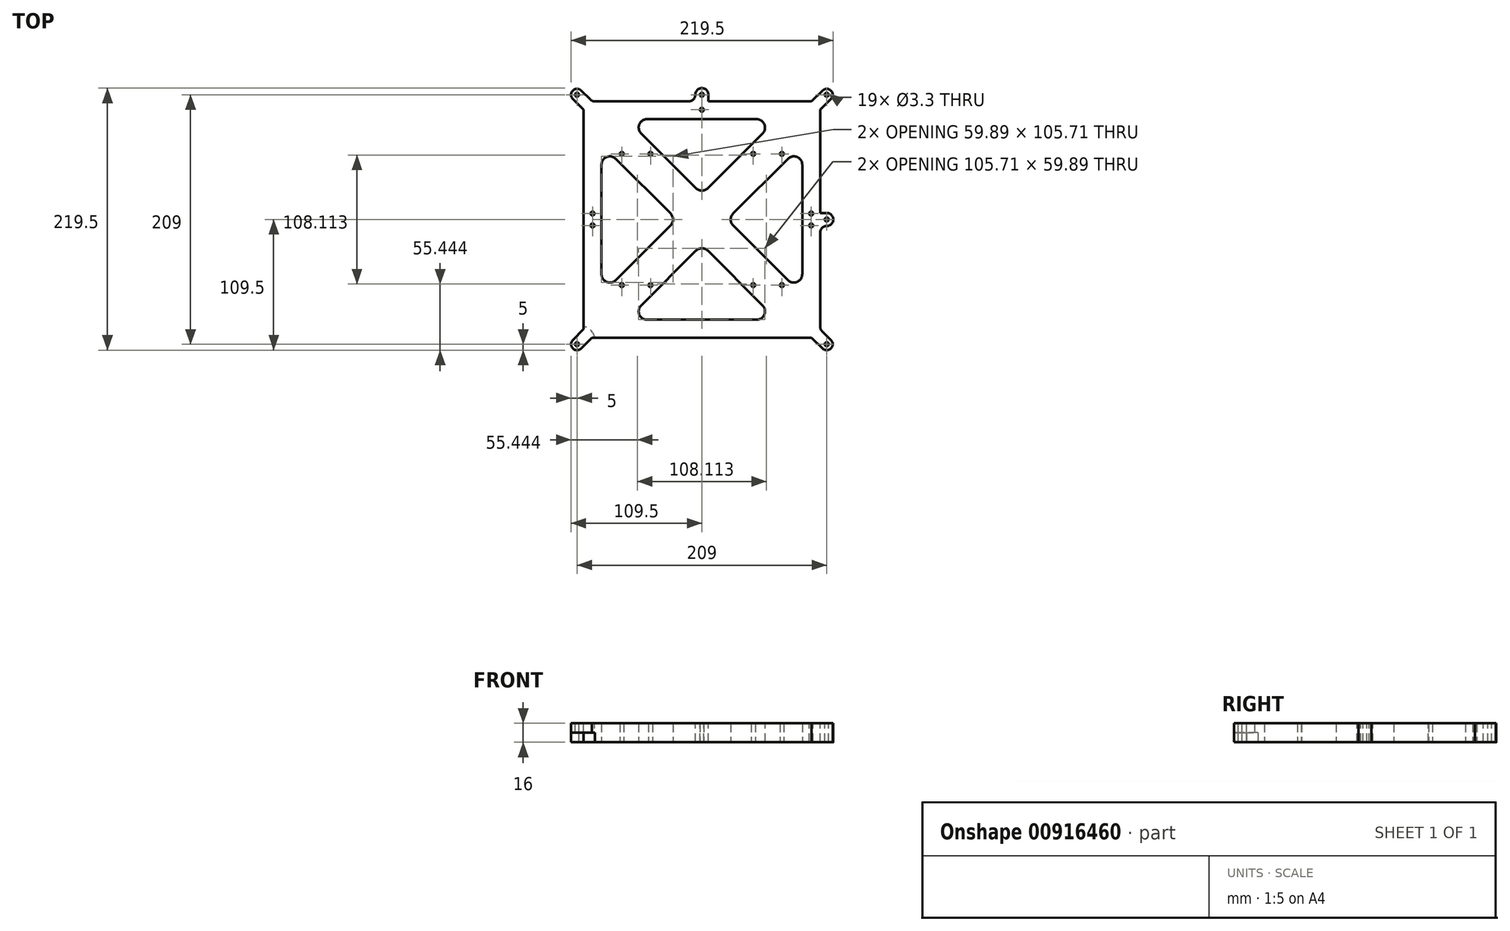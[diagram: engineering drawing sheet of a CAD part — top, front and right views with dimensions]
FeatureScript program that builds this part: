
annotation { "Feature Type Name" : "Feature", "Feature Type Description" : "" }
export const myFeature = defineFeature(function(context is Context, id is Id, definition is map)
    precondition{}
    {
        {
            var Q0;
            Q0=qCreatedBy(makeId("Top.planeOp"),FACE);
            var sketch = newSketch(context, id + "F0", { "sketchPlane" : qUnion([Q0])});
            skLineSegment(sketch, "E0.bottom", {"start": v(99, 99) * mm, "end": v(-99, 99) * mm});
            skLineSegment(sketch, "E0.top", {"start": v(99, -99) * mm, "end": v(-99, -99) * mm});
            skLineSegment(sketch, "E0.left", {"start": v(99, 99) * mm, "end": v(99, -99) * mm});
            skLineSegment(sketch, "E0.right", {"start": v(-99, 99) * mm, "end": v(-99, -99) * mm});
            skPoint(sketch, "E0.middle", {"position": v(0, 0) * mm});
            skLineSegment(sketch, "E1", {"start": v(99, 99) * mm, "end": v(-99, -99) * mm, "construction": true});
            skLineSegment(sketch, "E2", {"start": v(0, 21.21) * mm, "end": v(62.79, 84) * mm});
            skLineSegment(sketch, "E3.MirrorCS", {"start": v(0, 21.21) * mm, "end": v(-62.79, 84) * mm});
            skLineSegment(sketch, "E4", {"start": v(62.79, 84) * mm, "end": v(-62.79, 84) * mm});
            skLineSegment(sketch, "E5", {"start": v(-99, 99) * mm, "end": v(99, -99) * mm, "construction": true});
            skLineSegment(sketch, "E6.MirrorCS", {"start": v(-21.21, 0) * mm, "end": v(-84, 62.79) * mm});
            skLineSegment(sketch, "E7.MirrorCS", {"start": v(-84, -62.79) * mm, "end": v(-84, 62.79) * mm});
            skLineSegment(sketch, "E8.MirrorCS", {"start": v(-21.21, 0) * mm, "end": v(-84, -62.79) * mm});
            skLineSegment(sketch, "E9.MirrorCS", {"start": v(21.21, 0) * mm, "end": v(84, 62.79) * mm});
            skLineSegment(sketch, "E10.MirrorCS", {"start": v(84, 62.79) * mm, "end": v(84, -62.79) * mm});
            skLineSegment(sketch, "E11.MirrorCS", {"start": v(21.21, 0) * mm, "end": v(84, -62.79) * mm});
            skLineSegment(sketch, "E12.MirrorCS", {"start": v(0, -21.21) * mm, "end": v(-62.79, -84) * mm});
            skLineSegment(sketch, "E13.MirrorCS", {"start": v(0, -21.21) * mm, "end": v(62.79, -84) * mm});
            skLineSegment(sketch, "E14.MirrorCS", {"start": v(-62.79, -84) * mm, "end": v(62.79, -84) * mm});
            skLineSegment(sketch, "E15", {"start": v(-55, 55) * mm, "end": v(-43, 55) * mm, "construction": true});
            skLineSegment(sketch, "E16", {"start": v(-55, 55) * mm, "end": v(-67, 55) * mm, "construction": true});
            skLineSegment(sketch, "E17.MirrorCS", {"start": v(55, 55) * mm, "end": v(67, 55) * mm, "construction": true});
            skLineSegment(sketch, "E18.MirrorCS", {"start": v(55, 55) * mm, "end": v(43, 55) * mm, "construction": true});
            skLineSegment(sketch, "E19.MirrorCS", {"start": v(55, -55) * mm, "end": v(67, -55) * mm, "construction": true});
            skLineSegment(sketch, "E20.MirrorCS", {"start": v(-55, -55) * mm, "end": v(-43, -55) * mm, "construction": true});
            skLineSegment(sketch, "E21.MirrorCS", {"start": v(-55, -55) * mm, "end": v(-67, -55) * mm, "construction": true});
            skLineSegment(sketch, "E22.MirrorCS", {"start": v(55, -55) * mm, "end": v(43, -55) * mm, "construction": true});
            skSolve(sketch);
        }
        {
            var Q0;
            Q0=makeQuery(id+"F0.imprint","IMPRINT",FACE,{"disambiguationData":[TD([[makeQuery(id+"F0.imprint","IMPRINT",EDGE,{"derivedFrom":sQuery(id+"F0.wireOp",EDGE,"E0.bottom")}),1.0]])]});
            extrude(context, id + "F1", {"entities" : qUnion([Q0]), "depth" : 16 * mm});
        }
        {
            var Q0;
            Q0=makeQuery(id+"F1.opExtrude","CAP_FACE",FACE,{"disambiguationData":[OSD([sQuery(id+"F0.wireOp",EDGE,"E0.bottom"),sQuery(id+"F0.wireOp",EDGE,"E0.top"),sQuery(id+"F0.wireOp",EDGE,"E0.left"),sQuery(id+"F0.wireOp",EDGE,"E0.right"),sQuery(id+"F0.wireOp",EDGE,"E2"),sQuery(id+"F0.wireOp",EDGE,"E3.MirrorCS"),sQuery(id+"F0.wireOp",EDGE,"E4"),sQuery(id+"F0.wireOp",EDGE,"E6.MirrorCS"),sQuery(id+"F0.wireOp",EDGE,"E7.MirrorCS"),sQuery(id+"F0.wireOp",EDGE,"E8.MirrorCS"),sQuery(id+"F0.wireOp",EDGE,"E9.MirrorCS"),sQuery(id+"F0.wireOp",EDGE,"E10.MirrorCS"),sQuery(id+"F0.wireOp",EDGE,"E11.MirrorCS"),sQuery(id+"F0.wireOp",EDGE,"E12.MirrorCS"),sQuery(id+"F0.wireOp",EDGE,"E13.MirrorCS"),sQuery(id+"F0.wireOp",EDGE,"E14.MirrorCS")])],"isStart":false});
            var sketch = newSketch(context, id + "F2", { "sketchPlane" : qUnion([Q0])});
            skLineSegment(sketch, "E23", {"start": v(-99, 99) * mm, "end": v(-104.5, 104.5) * mm, "construction": true});
            skLineSegment(sketch, "E24.0", {"start": v(-91.93, 99) * mm, "end": v(-100.96, 108.04) * mm});
            skLineSegment(sketch, "E25.0", {"start": v(-99, 91.93) * mm, "end": v(-108.04, 100.96) * mm});
            skArc(sketch, "E26", {"start": v(-108.04, 100.96) * mm, "mid": v(-108.04, 108.04) * mm, "end": v(-100.96, 108.04) * mm});
            skLineSegment(sketch, "E27.MirrorCS", {"start": v(99, 91.93) * mm, "end": v(108.04, 100.96) * mm});
            skLineSegment(sketch, "E28.MirrorCS", {"start": v(99, 99) * mm, "end": v(104.5, 104.5) * mm, "construction": true});
            skLineSegment(sketch, "E29.MirrorCS", {"start": v(91.93, 99) * mm, "end": v(100.96, 108.04) * mm});
            skArc(sketch, "E30.MirrorCS", {"start": v(108.04, 100.96) * mm, "mid": v(108.04, 108.04) * mm, "end": v(100.96, 108.04) * mm});
            skLineSegment(sketch, "E31.MirrorCS", {"start": v(99, -99) * mm, "end": v(104.5, -104.5) * mm, "construction": true});
            skLineSegment(sketch, "E32.MirrorCS", {"start": v(-99, -99) * mm, "end": v(-104.5, -104.5) * mm, "construction": true});
            skLineSegment(sketch, "E33.MirrorCS", {"start": v(-99, -91.93) * mm, "end": v(-108.04, -100.96) * mm});
            skLineSegment(sketch, "E34.MirrorCS", {"start": v(91.93, -99) * mm, "end": v(100.96, -108.04) * mm});
            skArc(sketch, "E35.MirrorCS", {"start": v(108.04, -100.96) * mm, "mid": v(108.04, -108.04) * mm, "end": v(100.96, -108.04) * mm});
            skLineSegment(sketch, "E36.MirrorCS", {"start": v(99, -91.93) * mm, "end": v(108.04, -100.96) * mm});
            skArc(sketch, "E37.MirrorCS", {"start": v(-108.04, -100.96) * mm, "mid": v(-108.04, -108.04) * mm, "end": v(-100.96, -108.04) * mm});
            skLineSegment(sketch, "E38.MirrorCS", {"start": v(-91.93, -99) * mm, "end": v(-100.96, -108.04) * mm});
            skLineSegment(sketch, "E39", {"start": v(-5.5, 99) * mm, "end": v(-5.5, 110) * mm});
            skLineSegment(sketch, "E40", {"start": v(-5.5, 110) * mm, "end": v(5.5, 110) * mm});
            skLineSegment(sketch, "E41", {"start": v(5.5, 110) * mm, "end": v(5.5, 99) * mm});
            skLineSegment(sketch, "E42", {"start": v(99, 5.5) * mm, "end": v(110, 5.5) * mm});
            skLineSegment(sketch, "E43", {"start": v(110, 5.5) * mm, "end": v(110, -5.5) * mm});
            skLineSegment(sketch, "E44", {"start": v(110, -5.5) * mm, "end": v(99, -5.5) * mm});
            skLineSegment(sketch, "E45", {"start": v(110, 0) * mm, "end": v(99, 0) * mm, "construction": true});
            skLineSegment(sketch, "E46", {"start": v(0, 110) * mm, "end": v(0, 99) * mm, "construction": true});
            skLineSegment(sketch, "E47", {"start": v(0, 104.5) * mm, "end": v(5.5, 110) * mm, "construction": true});
            skLineSegment(sketch, "E48", {"start": v(104.5, 0) * mm, "end": v(110, -5.5) * mm, "construction": true});
            skLineSegment(sketch, "E49", {"start": v(91.5, 5) * mm, "end": v(91.5, -5) * mm});
            skLineSegment(sketch, "E50", {"start": v(-91.5, 5) * mm, "end": v(-91.5, -5) * mm});
            skSolve(sketch);
        }
        {
            var Q0;
            {var subQ4=sQuery(id+"F2.wireOp",EDGE,"E33.MirrorCS");Q0=makeQuery(id+"F2.imprint","IMPRINT",FACE,{"disambiguationData":[TD([[makeQuery(id+"F2.imprint","IMPRINT",EDGE,{"derivedFrom":subQ4}),1.0]])]});}
            var Q1;
            {var subQ3=sQuery(id+"F2.wireOp",EDGE,"E34.MirrorCS");Q1=makeQuery(id+"F2.imprint","IMPRINT",FACE,{"disambiguationData":[TD([[makeQuery(id+"F2.imprint","IMPRINT",EDGE,{"derivedFrom":subQ3}),1.0]])]});}
            var Q2;
            {var subQ0=sQuery(id+"F2.wireOp",EDGE,"E42");Q2=makeQuery(id+"F2.imprint","IMPRINT",FACE,{"disambiguationData":[TD([[makeQuery(id+"F2.imprint","IMPRINT",EDGE,{"derivedFrom":subQ0}),-1.0]])]});}
            var Q3;
            {var subQ4=sQuery(id+"F2.wireOp",EDGE,"E27.MirrorCS");Q3=makeQuery(id+"F2.imprint","IMPRINT",FACE,{"disambiguationData":[TD([[makeQuery(id+"F2.imprint","IMPRINT",EDGE,{"derivedFrom":subQ4}),1.0]])]});}
            var Q4;
            {var subQ3=sQuery(id+"F2.wireOp",EDGE,"E24.0");Q4=makeQuery(id+"F2.imprint","IMPRINT",FACE,{"disambiguationData":[TD([[makeQuery(id+"F2.imprint","IMPRINT",EDGE,{"derivedFrom":subQ3}),1.0]])]});}
            var Q5;
            {var subQ0=sQuery(id+"F2.wireOp",EDGE,"E39");Q5=makeQuery(id+"F2.imprint","IMPRINT",FACE,{"disambiguationData":[TD([[makeQuery(id+"F2.imprint","IMPRINT",EDGE,{"derivedFrom":subQ0}),-1.0]])]});}
            var Q6;
            Q6=makeQuery(id+"F1.opExtrude","CAP_FACE",FACE,{"disambiguationData":[OSD([sQuery(id+"F0.wireOp",EDGE,"E0.bottom"),sQuery(id+"F0.wireOp",EDGE,"E0.top"),sQuery(id+"F0.wireOp",EDGE,"E0.left"),sQuery(id+"F0.wireOp",EDGE,"E0.right"),sQuery(id+"F0.wireOp",EDGE,"E2"),sQuery(id+"F0.wireOp",EDGE,"E3.MirrorCS"),sQuery(id+"F0.wireOp",EDGE,"E4"),sQuery(id+"F0.wireOp",EDGE,"E6.MirrorCS"),sQuery(id+"F0.wireOp",EDGE,"E7.MirrorCS"),sQuery(id+"F0.wireOp",EDGE,"E8.MirrorCS"),sQuery(id+"F0.wireOp",EDGE,"E9.MirrorCS"),sQuery(id+"F0.wireOp",EDGE,"E10.MirrorCS"),sQuery(id+"F0.wireOp",EDGE,"E11.MirrorCS"),sQuery(id+"F0.wireOp",EDGE,"E12.MirrorCS"),sQuery(id+"F0.wireOp",EDGE,"E13.MirrorCS"),sQuery(id+"F0.wireOp",EDGE,"E14.MirrorCS")])],"isStart":true});
            extrude(context, id + "F3", {"entities" : qUnion([Q0, Q1, Q2, Q3, Q4, Q5]), "operationType" : NewBodyOperationType.ADD, "endBound" : BoundingType.UP_TO_SURFACE, "oppositeDirection" : true, "endBoundEntityFace" : qUnion([Q6]), "depth" : 25 * mm});
        }
        {
            var Q0;
            {var subQ0=sQuery(id+"F0.wireOp",EDGE,"E0.left");var subQ1=sQuery(id+"F0.wireOp",EDGE,"E14.MirrorCS");var subQ2=sQuery(id+"F0.wireOp",EDGE,"E13.MirrorCS");var subQ3=sQuery(id+"F0.wireOp",EDGE,"E12.MirrorCS");var subQ4=sQuery(id+"F0.wireOp",EDGE,"E11.MirrorCS");var subQ5=sQuery(id+"F0.wireOp",EDGE,"E10.MirrorCS");var subQ6=sQuery(id+"F0.wireOp",EDGE,"E9.MirrorCS");var subQ7=sQuery(id+"F0.wireOp",EDGE,"E8.MirrorCS");var subQ8=sQuery(id+"F0.wireOp",EDGE,"E7.MirrorCS");var subQ9=sQuery(id+"F0.wireOp",EDGE,"E6.MirrorCS");var subQ10=sQuery(id+"F0.wireOp",EDGE,"E4");var subQ11=sQuery(id+"F0.wireOp",EDGE,"E3.MirrorCS");var subQ12=sQuery(id+"F0.wireOp",EDGE,"E2");var subQ13=sQuery(id+"F0.wireOp",EDGE,"E0.right");var subQ14=sQuery(id+"F0.wireOp",EDGE,"E0.top");var subQ15=sQuery(id+"F0.wireOp",EDGE,"E0.bottom");Q0=makeQuery(id+"F3.boolean.opBoolean","MERGE",FACE,{"derivedFrom":[makeQuery(id+"F1.opExtrude","CAP_FACE",FACE,{"disambiguationData":[OSD([subQ15,subQ14,subQ0,subQ13,subQ12,subQ11,subQ10,subQ9,subQ8,subQ7,subQ6,subQ5,subQ4,subQ3,subQ2,subQ1])],"isStart":true}),makeQuery(id+"F3.opExtrude","CAP_FACE",FACE,{"disambiguationData":[OSD([subQ15,subQ14,subQ0,subQ13,subQ12,subQ11,subQ10,subQ9,subQ8,subQ7,subQ6,subQ5,subQ4,subQ3,subQ2,subQ1]),ownerDisambiguation([makeQuery(id+"F3.opExtrude","SWEPT_BODY",BODY,{"disambiguationData":[OSD([subQ15,subQ13,sQuery(id+"F2.wireOp",EDGE,"E24.0"),sQuery(id+"F2.wireOp",EDGE,"E25.0"),sQuery(id+"F2.wireOp",EDGE,"E26")])]})])],"isStart":false}),makeQuery(id+"F3.opExtrude","CAP_FACE",FACE,{"disambiguationData":[OSD([subQ15,subQ14,subQ0,subQ13,subQ12,subQ11,subQ10,subQ9,subQ8,subQ7,subQ6,subQ5,subQ4,subQ3,subQ2,subQ1]),ownerDisambiguation([makeQuery(id+"F3.opExtrude","SWEPT_BODY",BODY,{"disambiguationData":[OSD([subQ15,subQ0,sQuery(id+"F2.wireOp",EDGE,"E27.MirrorCS"),sQuery(id+"F2.wireOp",EDGE,"E29.MirrorCS"),sQuery(id+"F2.wireOp",EDGE,"E30.MirrorCS")])]})])],"isStart":false}),makeQuery(id+"F3.opExtrude","CAP_FACE",FACE,{"disambiguationData":[OSD([subQ15,subQ14,subQ0,subQ13,subQ12,subQ11,subQ10,subQ9,subQ8,subQ7,subQ6,subQ5,subQ4,subQ3,subQ2,subQ1]),ownerDisambiguation([makeQuery(id+"F3.opExtrude","SWEPT_BODY",BODY,{"disambiguationData":[OSD([subQ14,subQ13,sQuery(id+"F2.wireOp",EDGE,"E33.MirrorCS"),sQuery(id+"F2.wireOp",EDGE,"E37.MirrorCS"),sQuery(id+"F2.wireOp",EDGE,"E38.MirrorCS")])]})])],"isStart":false}),makeQuery(id+"F3.opExtrude","CAP_FACE",FACE,{"disambiguationData":[OSD([subQ15,subQ14,subQ0,subQ13,subQ12,subQ11,subQ10,subQ9,subQ8,subQ7,subQ6,subQ5,subQ4,subQ3,subQ2,subQ1]),ownerDisambiguation([makeQuery(id+"F3.opExtrude","SWEPT_BODY",BODY,{"disambiguationData":[OSD([subQ14,subQ0,sQuery(id+"F2.wireOp",EDGE,"E34.MirrorCS"),sQuery(id+"F2.wireOp",EDGE,"E35.MirrorCS"),sQuery(id+"F2.wireOp",EDGE,"E36.MirrorCS")])]})])],"isStart":false}),makeQuery(id+"F3.opExtrude","CAP_FACE",FACE,{"disambiguationData":[OSD([subQ15,subQ14,subQ0,subQ13,subQ12,subQ11,subQ10,subQ9,subQ8,subQ7,subQ6,subQ5,subQ4,subQ3,subQ2,subQ1]),ownerDisambiguation([makeQuery(id+"F3.opExtrude","SWEPT_BODY",BODY,{"disambiguationData":[OSD([subQ15,sQuery(id+"F2.wireOp",EDGE,"E39"),sQuery(id+"F2.wireOp",EDGE,"E40"),sQuery(id+"F2.wireOp",EDGE,"E41")])]})])],"isStart":false}),makeQuery(id+"F3.opExtrude","CAP_FACE",FACE,{"disambiguationData":[OSD([subQ15,subQ14,subQ0,subQ13,subQ12,subQ11,subQ10,subQ9,subQ8,subQ7,subQ6,subQ5,subQ4,subQ3,subQ2,subQ1]),ownerDisambiguation([makeQuery(id+"F3.opExtrude","SWEPT_BODY",BODY,{"disambiguationData":[OSD([subQ0,sQuery(id+"F2.wireOp",EDGE,"E42"),sQuery(id+"F2.wireOp",EDGE,"E43"),sQuery(id+"F2.wireOp",EDGE,"E44")])]})])],"isStart":false})]});}
            var sketch = newSketch(context, id + "F4", { "sketchPlane" : qUnion([Q0])});
            skPoint(sketch, "E51.0", {"position": v(-101.75, -101.75) * mm});
            skPoint(sketch, "E52.0", {"position": v(0, -104.5) * mm});
            skPoint(sketch, "E53.0", {"position": v(101.75, -101.75) * mm});
            skPoint(sketch, "E54.0", {"position": v(104.5, 0) * mm});
            skPoint(sketch, "E55.0", {"position": v(101.75, 101.75) * mm});
            skPoint(sketch, "E56.0", {"position": v(-101.75, 101.75) * mm});
            skCircle(sketch, "E57", {"center": v(-101.75, 101.75) * mm, "radius": 12.5 * mm});
            skCircle(sketch, "E58", {"center": v(101.75, 101.75) * mm, "radius": 12.5 * mm});
            skCircle(sketch, "E59", {"center": v(-101.75, -101.75) * mm, "radius": 12.5 * mm});
            skCircle(sketch, "E60", {"center": v(101.75, -101.75) * mm, "radius": 12.5 * mm});
            skCircle(sketch, "E61", {"center": v(0, -104.5) * mm, "radius": 10 * mm});
            skCircle(sketch, "E62", {"center": v(104.5, 0) * mm, "radius": 10 * mm});
            skLineSegment(sketch, "E63", {"start": v(-99, 0) * mm, "end": v(-84, 0) * mm});
            skCircle(sketch, "E64", {"center": v(0, -91.93) * mm, "radius": 2.5 * mm});
            skSolve(sketch);
        }
        {
            var Q0;
            {var subQ1=sQuery(id+"F0.wireOp",EDGE,"E0.top");var subQ6=sQuery(id+"F4.wireOp",EDGE,"E57");var subQ8=makeQuery(id+"F1.opExtrude","CAP_EDGE",EDGE,{"disambiguationData":[OSD([subQ1])],"isStart":true});var subQ9=makeQuery(id+"F4.imprint","INTERSECT",VERTEX,{"derivedFrom":[subQ8,subQ6]});Q0=makeQuery(id+"F4.imprint","IMPRINT",FACE,{"disambiguationData":[TD([[makeQuery(id+"F4.imprint","IMPRINT",EDGE,{"disambiguationData":[TD([[subQ9,1.0]])],"derivedFrom":subQ6}),1.0]])]});}
            var Q1;
            {var subQ1=sQuery(id+"F0.wireOp",EDGE,"E14.MirrorCS");var subQ2=sQuery(id+"F0.wireOp",EDGE,"E13.MirrorCS");var subQ3=sQuery(id+"F0.wireOp",EDGE,"E12.MirrorCS");var subQ4=sQuery(id+"F0.wireOp",EDGE,"E11.MirrorCS");var subQ5=sQuery(id+"F0.wireOp",EDGE,"E10.MirrorCS");var subQ6=sQuery(id+"F0.wireOp",EDGE,"E9.MirrorCS");var subQ7=sQuery(id+"F0.wireOp",EDGE,"E8.MirrorCS");var subQ8=sQuery(id+"F0.wireOp",EDGE,"E7.MirrorCS");var subQ9=sQuery(id+"F0.wireOp",EDGE,"E6.MirrorCS");var subQ10=sQuery(id+"F0.wireOp",EDGE,"E4");var subQ11=sQuery(id+"F0.wireOp",EDGE,"E3.MirrorCS");var subQ12=sQuery(id+"F0.wireOp",EDGE,"E2");var subQ13=sQuery(id+"F0.wireOp",EDGE,"E0.right");var subQ14=sQuery(id+"F0.wireOp",EDGE,"E0.left");var subQ15=sQuery(id+"F0.wireOp",EDGE,"E0.top");var subQ16=sQuery(id+"F0.wireOp",EDGE,"E0.bottom");var subQ17=makeQuery(id+"F1.opExtrude","CAP_FACE",FACE,{"disambiguationData":[OSD([subQ16,subQ15,subQ14,subQ13,subQ12,subQ11,subQ10,subQ9,subQ8,subQ7,subQ6,subQ5,subQ4,subQ3,subQ2,subQ1])],"isStart":true});var subQ22=sQuery(id+"F2.wireOp",EDGE,"E24.0");var subQ26=makeQuery(id+"F3.opExtrude","TWEAK_EDGE",EDGE,{"derivedFrom":[subQ17,makeQuery(id+"F2.imprint","IMPRINT",EDGE,{"derivedFrom":subQ22})]});Q1=makeQuery(id+"F4.imprint","IMPRINT",FACE,{"disambiguationData":[TD([[makeQuery(id+"F4.imprint","IMPRINT",EDGE,{"derivedFrom":subQ26}),1.0]])]});}
            var Q2;
            {var subQ1=sQuery(id+"F0.wireOp",EDGE,"E14.MirrorCS");var subQ2=sQuery(id+"F0.wireOp",EDGE,"E13.MirrorCS");var subQ3=sQuery(id+"F0.wireOp",EDGE,"E12.MirrorCS");var subQ4=sQuery(id+"F0.wireOp",EDGE,"E11.MirrorCS");var subQ5=sQuery(id+"F0.wireOp",EDGE,"E10.MirrorCS");var subQ6=sQuery(id+"F0.wireOp",EDGE,"E9.MirrorCS");var subQ7=sQuery(id+"F0.wireOp",EDGE,"E8.MirrorCS");var subQ8=sQuery(id+"F0.wireOp",EDGE,"E7.MirrorCS");var subQ9=sQuery(id+"F0.wireOp",EDGE,"E6.MirrorCS");var subQ10=sQuery(id+"F0.wireOp",EDGE,"E4");var subQ11=sQuery(id+"F0.wireOp",EDGE,"E3.MirrorCS");var subQ12=sQuery(id+"F0.wireOp",EDGE,"E2");var subQ13=sQuery(id+"F0.wireOp",EDGE,"E0.right");var subQ14=sQuery(id+"F0.wireOp",EDGE,"E0.left");var subQ15=sQuery(id+"F0.wireOp",EDGE,"E0.top");var subQ16=sQuery(id+"F0.wireOp",EDGE,"E0.bottom");var subQ17=makeQuery(id+"F1.opExtrude","CAP_FACE",FACE,{"disambiguationData":[OSD([subQ16,subQ15,subQ14,subQ13,subQ12,subQ11,subQ10,subQ9,subQ8,subQ7,subQ6,subQ5,subQ4,subQ3,subQ2,subQ1])],"isStart":true});var subQ18=sQuery(id+"F2.wireOp",EDGE,"E39");var subQ19=makeQuery(id+"F3.opExtrude","TWEAK_EDGE",EDGE,{"derivedFrom":[subQ17,makeQuery(id+"F2.imprint","IMPRINT",EDGE,{"derivedFrom":subQ18})]});Q2=makeQuery(id+"F4.imprint","IMPRINT",FACE,{"disambiguationData":[TD([[makeQuery(id+"F4.imprint","IMPRINT",EDGE,{"derivedFrom":subQ19}),-1.0]])]});}
            var Q3;
            {var subQ1=sQuery(id+"F0.wireOp",EDGE,"E14.MirrorCS");var subQ2=sQuery(id+"F0.wireOp",EDGE,"E13.MirrorCS");var subQ3=sQuery(id+"F0.wireOp",EDGE,"E12.MirrorCS");var subQ4=sQuery(id+"F0.wireOp",EDGE,"E11.MirrorCS");var subQ5=sQuery(id+"F0.wireOp",EDGE,"E10.MirrorCS");var subQ6=sQuery(id+"F0.wireOp",EDGE,"E9.MirrorCS");var subQ7=sQuery(id+"F0.wireOp",EDGE,"E8.MirrorCS");var subQ8=sQuery(id+"F0.wireOp",EDGE,"E7.MirrorCS");var subQ9=sQuery(id+"F0.wireOp",EDGE,"E6.MirrorCS");var subQ10=sQuery(id+"F0.wireOp",EDGE,"E4");var subQ11=sQuery(id+"F0.wireOp",EDGE,"E3.MirrorCS");var subQ12=sQuery(id+"F0.wireOp",EDGE,"E2");var subQ13=sQuery(id+"F0.wireOp",EDGE,"E0.right");var subQ14=sQuery(id+"F0.wireOp",EDGE,"E0.left");var subQ15=sQuery(id+"F0.wireOp",EDGE,"E0.top");var subQ16=sQuery(id+"F0.wireOp",EDGE,"E0.bottom");var subQ17=makeQuery(id+"F1.opExtrude","CAP_FACE",FACE,{"disambiguationData":[OSD([subQ16,subQ15,subQ14,subQ13,subQ12,subQ11,subQ10,subQ9,subQ8,subQ7,subQ6,subQ5,subQ4,subQ3,subQ2,subQ1])],"isStart":true});var subQ19=sQuery(id+"F2.wireOp",EDGE,"E42");var subQ20=makeQuery(id+"F3.opExtrude","TWEAK_EDGE",EDGE,{"derivedFrom":[subQ17,makeQuery(id+"F2.imprint","IMPRINT",EDGE,{"derivedFrom":subQ19})]});Q3=makeQuery(id+"F4.imprint","IMPRINT",FACE,{"disambiguationData":[TD([[makeQuery(id+"F4.imprint","IMPRINT",EDGE,{"derivedFrom":subQ20}),-1.0]])]});}
            var Q4;
            {var subQ1=sQuery(id+"F0.wireOp",EDGE,"E14.MirrorCS");var subQ2=sQuery(id+"F0.wireOp",EDGE,"E13.MirrorCS");var subQ3=sQuery(id+"F0.wireOp",EDGE,"E12.MirrorCS");var subQ4=sQuery(id+"F0.wireOp",EDGE,"E11.MirrorCS");var subQ5=sQuery(id+"F0.wireOp",EDGE,"E10.MirrorCS");var subQ6=sQuery(id+"F0.wireOp",EDGE,"E9.MirrorCS");var subQ7=sQuery(id+"F0.wireOp",EDGE,"E8.MirrorCS");var subQ8=sQuery(id+"F0.wireOp",EDGE,"E7.MirrorCS");var subQ9=sQuery(id+"F0.wireOp",EDGE,"E6.MirrorCS");var subQ10=sQuery(id+"F0.wireOp",EDGE,"E4");var subQ11=sQuery(id+"F0.wireOp",EDGE,"E3.MirrorCS");var subQ12=sQuery(id+"F0.wireOp",EDGE,"E2");var subQ13=sQuery(id+"F0.wireOp",EDGE,"E0.right");var subQ14=sQuery(id+"F0.wireOp",EDGE,"E0.left");var subQ15=sQuery(id+"F0.wireOp",EDGE,"E0.top");var subQ16=sQuery(id+"F0.wireOp",EDGE,"E0.bottom");var subQ17=makeQuery(id+"F1.opExtrude","CAP_FACE",FACE,{"disambiguationData":[OSD([subQ16,subQ15,subQ14,subQ13,subQ12,subQ11,subQ10,subQ9,subQ8,subQ7,subQ6,subQ5,subQ4,subQ3,subQ2,subQ1])],"isStart":true});var subQ19=sQuery(id+"F2.wireOp",EDGE,"E34.MirrorCS");var subQ20=makeQuery(id+"F3.opExtrude","TWEAK_EDGE",EDGE,{"derivedFrom":[subQ17,makeQuery(id+"F2.imprint","IMPRINT",EDGE,{"derivedFrom":subQ19})]});Q4=makeQuery(id+"F4.imprint","IMPRINT",FACE,{"disambiguationData":[TD([[makeQuery(id+"F4.imprint","IMPRINT",EDGE,{"derivedFrom":subQ20}),1.0]])]});}
            var Q5;
            {var subQ1=sQuery(id+"F0.wireOp",EDGE,"E14.MirrorCS");var subQ2=sQuery(id+"F0.wireOp",EDGE,"E13.MirrorCS");var subQ3=sQuery(id+"F0.wireOp",EDGE,"E12.MirrorCS");var subQ4=sQuery(id+"F0.wireOp",EDGE,"E11.MirrorCS");var subQ5=sQuery(id+"F0.wireOp",EDGE,"E10.MirrorCS");var subQ6=sQuery(id+"F0.wireOp",EDGE,"E9.MirrorCS");var subQ7=sQuery(id+"F0.wireOp",EDGE,"E8.MirrorCS");var subQ8=sQuery(id+"F0.wireOp",EDGE,"E7.MirrorCS");var subQ9=sQuery(id+"F0.wireOp",EDGE,"E6.MirrorCS");var subQ10=sQuery(id+"F0.wireOp",EDGE,"E4");var subQ11=sQuery(id+"F0.wireOp",EDGE,"E3.MirrorCS");var subQ12=sQuery(id+"F0.wireOp",EDGE,"E2");var subQ13=sQuery(id+"F0.wireOp",EDGE,"E0.right");var subQ14=sQuery(id+"F0.wireOp",EDGE,"E0.left");var subQ15=sQuery(id+"F0.wireOp",EDGE,"E0.top");var subQ16=sQuery(id+"F0.wireOp",EDGE,"E0.bottom");var subQ17=makeQuery(id+"F1.opExtrude","CAP_FACE",FACE,{"disambiguationData":[OSD([subQ16,subQ15,subQ14,subQ13,subQ12,subQ11,subQ10,subQ9,subQ8,subQ7,subQ6,subQ5,subQ4,subQ3,subQ2,subQ1])],"isStart":true});var subQ23=sQuery(id+"F2.wireOp",EDGE,"E27.MirrorCS");var subQ34=makeQuery(id+"F3.opExtrude","TWEAK_EDGE",EDGE,{"derivedFrom":[subQ17,makeQuery(id+"F2.imprint","IMPRINT",EDGE,{"derivedFrom":subQ23})]});Q5=makeQuery(id+"F4.imprint","IMPRINT",FACE,{"disambiguationData":[TD([[makeQuery(id+"F4.imprint","IMPRINT",EDGE,{"derivedFrom":subQ34}),1.0]])]});}
            extrude(context, id + "F5", {"entities" : qUnion([Q0, Q1, Q2, Q3, Q4, Q5]), "operationType" : NewBodyOperationType.REMOVE, "oppositeDirection" : true, "depth" : 8 * mm});
        }
        {
            var Q0;
            Q0=makeQuery(id+"F3.opExtrude","SWEPT_EDGE",EDGE,{"disambiguationData":[OSD([sQuery(id+"F0.wireOp",EDGE,"E0.bottom"),sQuery(id+"F2.wireOp",EDGE,"E24.0")])]});
            var Q1;
            Q1=makeQuery(id+"F3.opExtrude","SWEPT_EDGE",EDGE,{"disambiguationData":[OSD([sQuery(id+"F0.wireOp",EDGE,"E0.right"),sQuery(id+"F2.wireOp",EDGE,"E25.0")])]});
            var Q2;
            Q2=makeQuery(id+"F3.opExtrude","SWEPT_EDGE",EDGE,{"disambiguationData":[OSD([sQuery(id+"F0.wireOp",EDGE,"E0.right"),sQuery(id+"F2.wireOp",EDGE,"E33.MirrorCS")])]});
            var Q3;
            Q3=makeQuery(id+"F3.opExtrude","SWEPT_EDGE",EDGE,{"disambiguationData":[OSD([sQuery(id+"F0.wireOp",EDGE,"E0.top"),sQuery(id+"F2.wireOp",EDGE,"E38.MirrorCS")])]});
            var Q4;
            Q4=makeQuery(id+"F3.opExtrude","SWEPT_EDGE",EDGE,{"disambiguationData":[OSD([sQuery(id+"F0.wireOp",EDGE,"E0.top"),sQuery(id+"F2.wireOp",EDGE,"E34.MirrorCS")])]});
            var Q5;
            Q5=makeQuery(id+"F3.opExtrude","SWEPT_EDGE",EDGE,{"disambiguationData":[OSD([sQuery(id+"F0.wireOp",EDGE,"E0.left"),sQuery(id+"F2.wireOp",EDGE,"E36.MirrorCS")])]});
            var Q6;
            Q6=makeQuery(id+"F3.opExtrude","SWEPT_EDGE",EDGE,{"disambiguationData":[OSD([sQuery(id+"F0.wireOp",EDGE,"E0.left"),sQuery(id+"F2.wireOp",EDGE,"E27.MirrorCS")])]});
            var Q7;
            Q7=makeQuery(id+"F3.opExtrude","SWEPT_EDGE",EDGE,{"disambiguationData":[OSD([sQuery(id+"F0.wireOp",EDGE,"E0.bottom"),sQuery(id+"F2.wireOp",EDGE,"E29.MirrorCS")])]});
            var Q8;
            Q8=makeQuery(id+"F5.boolean.opBoolean","COPY",EDGE,{"derivedFrom":makeQuery(id+"F5.opExtrude","SWEPT_EDGE",EDGE,{"disambiguationData":[OSD([sQuery(id+"F0.wireOp",EDGE,"E0.bottom"),sQuery(id+"F4.wireOp",EDGE,"E60")])]})});
            var Q9;
            Q9=makeQuery(id+"F5.boolean.opBoolean","COPY",EDGE,{"derivedFrom":makeQuery(id+"F5.opExtrude","SWEPT_EDGE",EDGE,{"disambiguationData":[OSD([sQuery(id+"F0.wireOp",EDGE,"E0.left"),sQuery(id+"F4.wireOp",EDGE,"E60")])]})});
            var Q10;
            Q10=makeQuery(id+"F5.boolean.opBoolean","COPY",EDGE,{"derivedFrom":makeQuery(id+"F5.opExtrude","SWEPT_EDGE",EDGE,{"disambiguationData":[OSD([sQuery(id+"F0.wireOp",EDGE,"E0.left"),sQuery(id+"F4.wireOp",EDGE,"E58")])]})});
            var Q11;
            Q11=makeQuery(id+"F5.boolean.opBoolean","COPY",EDGE,{"derivedFrom":makeQuery(id+"F5.opExtrude","SWEPT_EDGE",EDGE,{"disambiguationData":[OSD([sQuery(id+"F0.wireOp",EDGE,"E0.top"),sQuery(id+"F4.wireOp",EDGE,"E58")])]})});
            var Q12;
            Q12=makeQuery(id+"F5.boolean.opBoolean","COPY",EDGE,{"derivedFrom":makeQuery(id+"F5.opExtrude","SWEPT_EDGE",EDGE,{"disambiguationData":[OSD([sQuery(id+"F0.wireOp",EDGE,"E0.top"),sQuery(id+"F4.wireOp",EDGE,"E57")])]})});
            var Q13;
            Q13=makeQuery(id+"F5.boolean.opBoolean","COPY",EDGE,{"derivedFrom":makeQuery(id+"F5.opExtrude","SWEPT_EDGE",EDGE,{"disambiguationData":[OSD([sQuery(id+"F0.wireOp",EDGE,"E0.right"),sQuery(id+"F4.wireOp",EDGE,"E57")])]})});
            var Q14;
            Q14=makeQuery(id+"F5.boolean.opBoolean","COPY",EDGE,{"derivedFrom":makeQuery(id+"F5.opExtrude","SWEPT_EDGE",EDGE,{"disambiguationData":[OSD([sQuery(id+"F0.wireOp",EDGE,"E0.bottom"),sQuery(id+"F4.wireOp",EDGE,"E59")])]})});
            var Q15;
            Q15=makeQuery(id+"F5.boolean.opBoolean","COPY",EDGE,{"derivedFrom":makeQuery(id+"F5.opExtrude","SWEPT_EDGE",EDGE,{"disambiguationData":[OSD([sQuery(id+"F0.wireOp",EDGE,"E0.right"),sQuery(id+"F4.wireOp",EDGE,"E59")])]})});
            fillet(context, id + "F6", {"entities" : qUnion([Q0, Q1, Q2, Q3, Q4, Q5, Q6, Q7, Q8, Q9, Q10, Q11, Q12, Q13, Q14, Q15]), "radius" : 5 * mm, "tangentPropagation" : true, "allowEdgeOverflow" : false});
        }
        {
            var Q0;
            Q0=makeQuery(id+"F1.opExtrude","SWEPT_EDGE",EDGE,{"disambiguationData":[OSD([sQuery(id+"F0.wireOp",EDGE,"E7.MirrorCS"),sQuery(id+"F0.wireOp",EDGE,"E8.MirrorCS")])]});
            var Q1;
            Q1=makeQuery(id+"F1.opExtrude","SWEPT_EDGE",EDGE,{"disambiguationData":[OSD([sQuery(id+"F0.wireOp",EDGE,"E6.MirrorCS"),sQuery(id+"F0.wireOp",EDGE,"E7.MirrorCS")])]});
            var Q2;
            Q2=makeQuery(id+"F1.opExtrude","SWEPT_EDGE",EDGE,{"disambiguationData":[OSD([sQuery(id+"F0.wireOp",EDGE,"E6.MirrorCS"),sQuery(id+"F0.wireOp",EDGE,"E8.MirrorCS")])]});
            var Q3;
            Q3=makeQuery(id+"F1.opExtrude","SWEPT_EDGE",EDGE,{"disambiguationData":[OSD([sQuery(id+"F0.wireOp",EDGE,"E13.MirrorCS"),sQuery(id+"F0.wireOp",EDGE,"E14.MirrorCS")])]});
            var Q4;
            Q4=makeQuery(id+"F1.opExtrude","SWEPT_EDGE",EDGE,{"disambiguationData":[OSD([sQuery(id+"F0.wireOp",EDGE,"E12.MirrorCS"),sQuery(id+"F0.wireOp",EDGE,"E14.MirrorCS")])]});
            var Q5;
            Q5=makeQuery(id+"F1.opExtrude","SWEPT_EDGE",EDGE,{"disambiguationData":[OSD([sQuery(id+"F0.wireOp",EDGE,"E12.MirrorCS"),sQuery(id+"F0.wireOp",EDGE,"E13.MirrorCS")])]});
            var Q6;
            Q6=makeQuery(id+"F1.opExtrude","SWEPT_EDGE",EDGE,{"disambiguationData":[OSD([sQuery(id+"F0.wireOp",EDGE,"E9.MirrorCS"),sQuery(id+"F0.wireOp",EDGE,"E11.MirrorCS")])]});
            var Q7;
            Q7=makeQuery(id+"F1.opExtrude","SWEPT_EDGE",EDGE,{"disambiguationData":[OSD([sQuery(id+"F0.wireOp",EDGE,"E10.MirrorCS"),sQuery(id+"F0.wireOp",EDGE,"E11.MirrorCS")])]});
            var Q8;
            Q8=makeQuery(id+"F1.opExtrude","SWEPT_EDGE",EDGE,{"disambiguationData":[OSD([sQuery(id+"F0.wireOp",EDGE,"E9.MirrorCS"),sQuery(id+"F0.wireOp",EDGE,"E10.MirrorCS")])]});
            var Q9;
            Q9=makeQuery(id+"F1.opExtrude","SWEPT_EDGE",EDGE,{"disambiguationData":[OSD([sQuery(id+"F0.wireOp",EDGE,"E2"),sQuery(id+"F0.wireOp",EDGE,"E4")])]});
            var Q10;
            Q10=makeQuery(id+"F1.opExtrude","SWEPT_EDGE",EDGE,{"disambiguationData":[OSD([sQuery(id+"F0.wireOp",EDGE,"E2"),sQuery(id+"F0.wireOp",EDGE,"E3.MirrorCS")])]});
            var Q11;
            Q11=makeQuery(id+"F1.opExtrude","SWEPT_EDGE",EDGE,{"disambiguationData":[OSD([sQuery(id+"F0.wireOp",EDGE,"E3.MirrorCS"),sQuery(id+"F0.wireOp",EDGE,"E4")])]});
            fillet(context, id + "F7", {"entities" : qUnion([Q0, Q1, Q2, Q3, Q4, Q5, Q6, Q7, Q8, Q9, Q10, Q11]), "radius" : 7 * mm, "tangentPropagation" : true, "allowEdgeOverflow" : false});
        }
        {
            var Q0;
            Q0=makeQuery(id+"F3.opExtrude","SWEPT_EDGE",EDGE,{"disambiguationData":[OSD([sQuery(id+"F0.wireOp",EDGE,"E0.left"),sQuery(id+"F2.wireOp",EDGE,"E44")])]});
            var Q1;
            Q1=makeQuery(id+"F3.opExtrude","SWEPT_EDGE",EDGE,{"disambiguationData":[OSD([sQuery(id+"F2.wireOp",EDGE,"E43"),sQuery(id+"F2.wireOp",EDGE,"E44")])]});
            var Q2;
            Q2=makeQuery(id+"F3.opExtrude","SWEPT_EDGE",EDGE,{"disambiguationData":[OSD([sQuery(id+"F2.wireOp",EDGE,"E42"),sQuery(id+"F2.wireOp",EDGE,"E43")])]});
            var Q3;
            Q3=makeQuery(id+"F3.opExtrude","SWEPT_EDGE",EDGE,{"disambiguationData":[OSD([sQuery(id+"F0.wireOp",EDGE,"E0.left"),sQuery(id+"F2.wireOp",EDGE,"E42")])]});
            var Q4;
            Q4=makeQuery(id+"F3.opExtrude","SWEPT_EDGE",EDGE,{"disambiguationData":[OSD([sQuery(id+"F2.wireOp",EDGE,"E39"),sQuery(id+"F2.wireOp",EDGE,"E40")])]});
            var Q5;
            Q5=makeQuery(id+"F3.opExtrude","SWEPT_EDGE",EDGE,{"disambiguationData":[OSD([sQuery(id+"F2.wireOp",EDGE,"E40"),sQuery(id+"F2.wireOp",EDGE,"E41")])]});
            var Q6;
            Q6=makeQuery(id+"F3.opExtrude","SWEPT_EDGE",EDGE,{"disambiguationData":[OSD([sQuery(id+"F0.wireOp",EDGE,"E0.bottom"),sQuery(id+"F2.wireOp",EDGE,"E39")])]});
            var Q7;
            Q7=makeQuery(id+"F3.opExtrude","SWEPT_EDGE",EDGE,{"disambiguationData":[OSD([sQuery(id+"F0.wireOp",EDGE,"E0.bottom"),sQuery(id+"F2.wireOp",EDGE,"E41")])]});
            fillet(context, id + "F8", {"entities" : qUnion([Q0, Q1, Q2, Q3, Q4, Q5, Q6, Q7]), "radius" : 5.5 * mm, "tangentPropagation" : true, "allowEdgeOverflow" : false});
        }
        {
            var Q0;
            Q0=sQuery(id+"F2.wireOp",VERTEX,"E28.MirrorCS.end");
            var Q1;
            Q1=sQuery(id+"F2.wireOp",VERTEX,"E23.end");
            var Q2;
            Q2=sQuery(id+"F2.wireOp",VERTEX,"E37.MirrorCS.center");
            var Q3;
            Q3=sQuery(id+"F2.wireOp",VERTEX,"E31.MirrorCS.end");
            var Q4;
            Q4=sQuery(id+"F2.wireOp",VERTEX,"2pDlAgmg-oWPr-uHAD-QSet-lFzdziWOcZdJ.end");
            var Q5;
            Q5=sQuery(id+"F2.wireOp",VERTEX,"dYqIcZGR-570r-Ir1H-HWpK-BYmHNwuklspW.end");
            var Q6;
            Q6=sQuery(id+"F2.wireOp",VERTEX,"E47.start");
            var Q7;
            Q7=sQuery(id+"F2.wireOp",VERTEX,"E48.start");
            var Q8;
            Q8=sQuery(id+"F2.wireOp",VERTEX,"E49.end");
            var Q9;
            Q9=sQuery(id+"F2.wireOp",VERTEX,"E49.start");
            var Q10;
            Q10=sQuery(id+"F2.wireOp",VERTEX,"E50.end");
            var Q11;
            Q11=sQuery(id+"F2.wireOp",VERTEX,"E50.start");
            var Q12;
            Q12=makeQuery(id+"F1.opExtrude","SWEPT_BODY",BODY,{"disambiguationData":[OSD([sQuery(id+"F0.wireOp",EDGE,"E0.bottom"),sQuery(id+"F0.wireOp",EDGE,"E0.top"),sQuery(id+"F0.wireOp",EDGE,"E0.left"),sQuery(id+"F0.wireOp",EDGE,"E0.right"),sQuery(id+"F0.wireOp",EDGE,"E2"),sQuery(id+"F0.wireOp",EDGE,"E3.MirrorCS"),sQuery(id+"F0.wireOp",EDGE,"E4"),sQuery(id+"F0.wireOp",EDGE,"E6.MirrorCS"),sQuery(id+"F0.wireOp",EDGE,"E7.MirrorCS"),sQuery(id+"F0.wireOp",EDGE,"E8.MirrorCS"),sQuery(id+"F0.wireOp",EDGE,"E9.MirrorCS"),sQuery(id+"F0.wireOp",EDGE,"E10.MirrorCS"),sQuery(id+"F0.wireOp",EDGE,"E11.MirrorCS"),sQuery(id+"F0.wireOp",EDGE,"E12.MirrorCS"),sQuery(id+"F0.wireOp",EDGE,"E13.MirrorCS"),sQuery(id+"F0.wireOp",EDGE,"E14.MirrorCS")])]});
            hole(context, id + "F9", {"style" : HoleStyle.SIMPLE, "endStyle" : HoleEndStyle.THROUGH, "holeDiameter" : 3.3 * mm, "majorDiameter" : 5 * mm, "tappedDepth" : 12 * mm, "tapClearance" : 3, "locations" : qUnion([Q0, Q1, Q2, Q3, Q4, Q5, Q6, Q7, Q8, Q9, Q10, Q11]), "scope" : qUnion([Q12])});
        }
        {
            var Q0;
            Q0=sQuery(id+"F0.wireOp",VERTEX,"E19.MirrorCS.end");
            var Q1;
            Q1=sQuery(id+"F0.wireOp",VERTEX,"E22.MirrorCS.end");
            var Q2;
            Q2=sQuery(id+"F0.wireOp",VERTEX,"E20.MirrorCS.end");
            var Q3;
            Q3=sQuery(id+"F0.wireOp",VERTEX,"E21.MirrorCS.end");
            var Q4;
            Q4=sQuery(id+"F0.wireOp",VERTEX,"E16.end");
            var Q5;
            Q5=sQuery(id+"F0.wireOp",VERTEX,"E15.end");
            var Q6;
            Q6=sQuery(id+"F0.wireOp",VERTEX,"E18.MirrorCS.end");
            var Q7;
            Q7=sQuery(id+"F0.wireOp",VERTEX,"E17.MirrorCS.end");
            var Q8;
            Q8=makeQuery(id+"F1.opExtrude","SWEPT_BODY",BODY,{"disambiguationData":[OSD([sQuery(id+"F0.wireOp",EDGE,"E0.bottom"),sQuery(id+"F0.wireOp",EDGE,"E0.top"),sQuery(id+"F0.wireOp",EDGE,"E0.left"),sQuery(id+"F0.wireOp",EDGE,"E0.right"),sQuery(id+"F0.wireOp",EDGE,"E2"),sQuery(id+"F0.wireOp",EDGE,"E3.MirrorCS"),sQuery(id+"F0.wireOp",EDGE,"E4"),sQuery(id+"F0.wireOp",EDGE,"E6.MirrorCS"),sQuery(id+"F0.wireOp",EDGE,"E7.MirrorCS"),sQuery(id+"F0.wireOp",EDGE,"E8.MirrorCS"),sQuery(id+"F0.wireOp",EDGE,"E9.MirrorCS"),sQuery(id+"F0.wireOp",EDGE,"E10.MirrorCS"),sQuery(id+"F0.wireOp",EDGE,"E11.MirrorCS"),sQuery(id+"F0.wireOp",EDGE,"E12.MirrorCS"),sQuery(id+"F0.wireOp",EDGE,"E13.MirrorCS"),sQuery(id+"F0.wireOp",EDGE,"E14.MirrorCS")])]});
            hole(context, id + "F10", {"style" : HoleStyle.SIMPLE, "endStyle" : HoleEndStyle.THROUGH, "oppositeDirection" : true, "standardTappedOrClearance" : lookupTablePath({ "standard" : "ISO", "fit" : "Normal", "size" : "M3", "type" : "Clearance" }), "standardBlindInLast" : lookupTablePath({ "fit" : "Standard", "standard" : "ISO", "size" : "M3", "type" : "Clearance" }), "holeDiameter" : 3.3 * mm, "tappedDepth" : 12 * mm, "tapClearance" : 3, "locations" : qUnion([Q0, Q1, Q2, Q3, Q4, Q5, Q6, Q7]), "scope" : qUnion([Q8])});
        }
        {
            var Q0;
            Q0=sQuery(id+"F4.wireOp",VERTEX,"E64.center");
            var Q1;
            Q1=makeQuery(id+"F1.opExtrude","SWEPT_BODY",BODY,{"disambiguationData":[OSD([sQuery(id+"F0.wireOp",EDGE,"E0.bottom"),sQuery(id+"F0.wireOp",EDGE,"E0.top"),sQuery(id+"F0.wireOp",EDGE,"E0.left"),sQuery(id+"F0.wireOp",EDGE,"E0.right"),sQuery(id+"F0.wireOp",EDGE,"E2"),sQuery(id+"F0.wireOp",EDGE,"E3.MirrorCS"),sQuery(id+"F0.wireOp",EDGE,"E4"),sQuery(id+"F0.wireOp",EDGE,"E6.MirrorCS"),sQuery(id+"F0.wireOp",EDGE,"E7.MirrorCS"),sQuery(id+"F0.wireOp",EDGE,"E8.MirrorCS"),sQuery(id+"F0.wireOp",EDGE,"E9.MirrorCS"),sQuery(id+"F0.wireOp",EDGE,"E10.MirrorCS"),sQuery(id+"F0.wireOp",EDGE,"E11.MirrorCS"),sQuery(id+"F0.wireOp",EDGE,"E12.MirrorCS"),sQuery(id+"F0.wireOp",EDGE,"E13.MirrorCS"),sQuery(id+"F0.wireOp",EDGE,"E14.MirrorCS")])]});
            hole(context, id + "F11", {"style" : HoleStyle.SIMPLE, "endStyle" : HoleEndStyle.THROUGH, "standardTappedOrClearance" : lookupTablePath({ "standard" : "ISO", "fit" : "Normal", "size" : "M3", "type" : "Clearance" }), "standardBlindInLast" : lookupTablePath({ "fit" : "Standard", "standard" : "ISO", "size" : "M3", "type" : "Clearance" }), "holeDiameter" : 3.3 * mm, "tappedDepth" : 12 * mm, "tapClearance" : 3, "locations" : qUnion([Q0]), "scope" : qUnion([Q1])});
        }
    });
